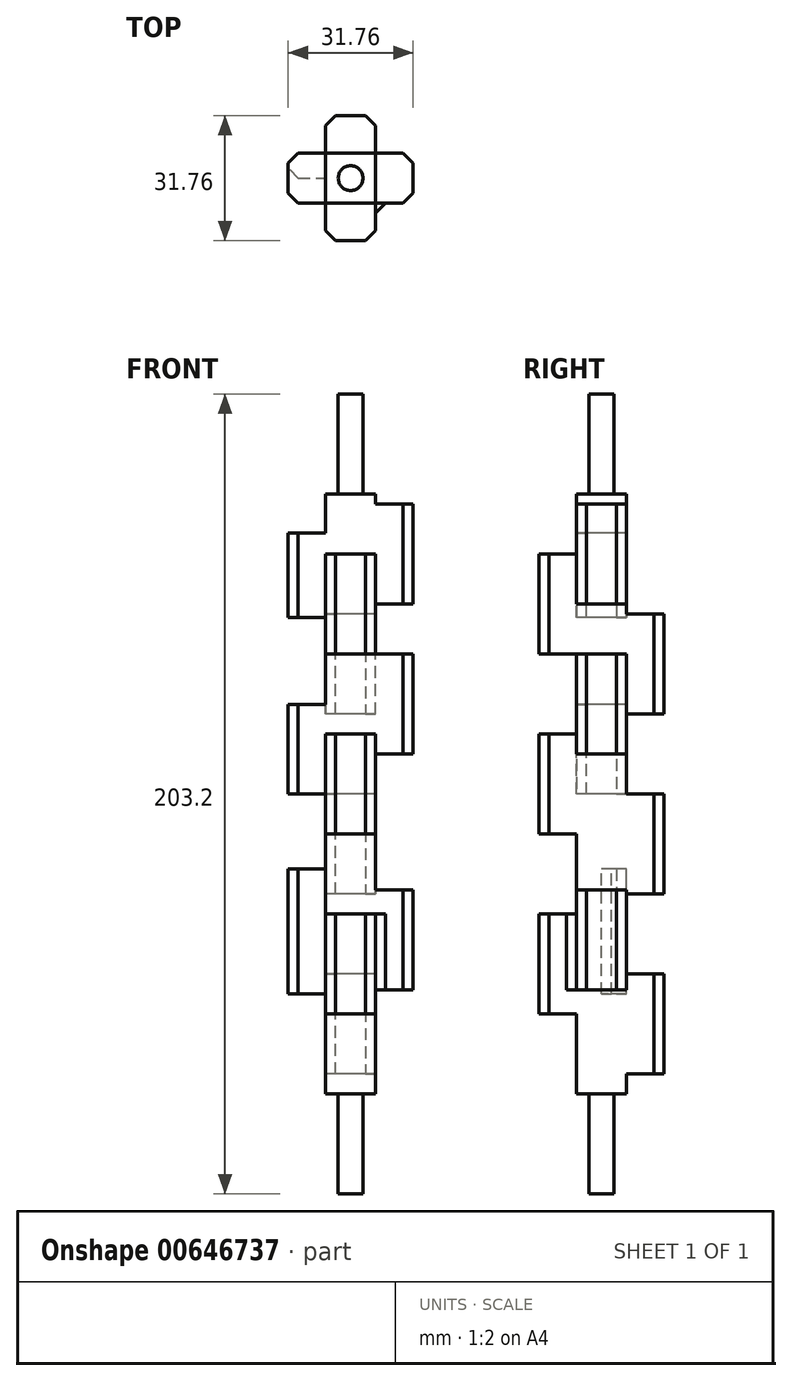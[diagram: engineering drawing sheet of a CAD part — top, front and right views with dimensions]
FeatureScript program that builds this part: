
annotation { "Feature Type Name" : "Feature", "Feature Type Description" : "" }
export const myFeature = defineFeature(function(context is Context, id is Id, definition is map)
    precondition{}
    {
        {
            var Q0;
            Q0=qCreatedBy(makeId("Top.planeOp"),FACE);
            var sketch = newSketch(context, id + "F0", { "sketchPlane" : qUnion([Q0])});
            skLineSegment(sketch, "E0.bottom", {"start": v(6.35, -6.35) * mm, "end": v(-6.35, -6.35) * mm});
            skLineSegment(sketch, "E0.top", {"start": v(6.35, 6.35) * mm, "end": v(-6.35, 6.35) * mm});
            skLineSegment(sketch, "E0.left", {"start": v(6.35, -6.35) * mm, "end": v(6.35, 6.35) * mm});
            skLineSegment(sketch, "E0.right", {"start": v(-6.35, -6.35) * mm, "end": v(-6.35, 6.35) * mm});
            skPoint(sketch, "E0.middle", {"position": v(0, 0) * mm});
            skSolve(sketch);
        }
        {
            var Q0;
            Q0=makeQuery(id+"F0.imprint","IMPRINT",FACE,{"disambiguationData":[TD([[makeQuery(id+"F0.imprint","IMPRINT",EDGE,{"derivedFrom":sQuery(id+"F0.wireOp",EDGE,"E0.bottom")}),-1.0]])]});
            extrude(context, id + "F1", {"entities" : qUnion([Q0]), "endBound" : BoundingType.SYMMETRIC, "depth" : 152.4 * mm, "offsetDistance" : 25.4 * mm});
        }
        {
            var Q0;
            Q0=makeQuery(id+"F1.opExtrude","SWEPT_FACE",FACE,{"disambiguationData":[OSD([sQuery(id+"F0.wireOp",EDGE,"E0.top")])]});
            var sketch = newSketch(context, id + "F2", { "sketchPlane" : qUnion([Q0])});
            skLineSegment(sketch, "E1.bottom", {"start": v(-6.35, 45.72) * mm, "end": v(6.35, 45.72) * mm});
            skLineSegment(sketch, "E1.top", {"start": v(-6.35, 20.32) * mm, "end": v(6.35, 20.32) * mm});
            skLineSegment(sketch, "E1.left", {"start": v(-6.35, 45.72) * mm, "end": v(-6.35, 20.32) * mm});
            skLineSegment(sketch, "E1.right", {"start": v(6.35, 45.72) * mm, "end": v(6.35, 20.32) * mm});
            skLineSegment(sketch, "E2.bottom", {"start": v(-6.35, 0) * mm, "end": v(6.35, 0) * mm});
            skLineSegment(sketch, "E2.top", {"start": v(-6.35, -25.4) * mm, "end": v(6.35, -25.4) * mm});
            skLineSegment(sketch, "E2.left", {"start": v(-6.35, 0) * mm, "end": v(-6.35, -25.4) * mm});
            skLineSegment(sketch, "E2.right", {"start": v(6.35, 0) * mm, "end": v(6.35, -25.4) * mm});
            skLineSegment(sketch, "E3.bottom", {"start": v(-6.35, -45.72) * mm, "end": v(6.35, -45.72) * mm});
            skLineSegment(sketch, "E3.top", {"start": v(-6.35, -71.12) * mm, "end": v(6.35, -71.12) * mm});
            skLineSegment(sketch, "E3.left", {"start": v(-6.35, -45.72) * mm, "end": v(-6.35, -71.12) * mm});
            skLineSegment(sketch, "E3.right", {"start": v(6.35, -45.72) * mm, "end": v(6.35, -71.12) * mm});
            skSolve(sketch);
        }
        {
            var Q0;
            Q0=makeQuery(id+"F2.imprint","IMPRINT",FACE,{"disambiguationData":[TD([[makeQuery(id+"F2.imprint","IMPRINT",EDGE,{"derivedFrom":sQuery(id+"F2.wireOp",EDGE,"E3.bottom")}),-1.0]])]});
            var Q1;
            Q1=makeQuery(id+"F2.imprint","IMPRINT",FACE,{"disambiguationData":[TD([[makeQuery(id+"F2.imprint","IMPRINT",EDGE,{"derivedFrom":sQuery(id+"F2.wireOp",EDGE,"E2.bottom")}),-1.0]])]});
            var Q2;
            Q2=makeQuery(id+"F2.imprint","IMPRINT",FACE,{"disambiguationData":[TD([[makeQuery(id+"F2.imprint","IMPRINT",EDGE,{"derivedFrom":sQuery(id+"F2.wireOp",EDGE,"E1.bottom")}),-1.0]])]});
            extrude(context, id + "F3", {"entities" : qUnion([Q0, Q1, Q2]), "operationType" : NewBodyOperationType.ADD, "depth" : 9.52 * mm, "offsetDistance" : 25.4 * mm});
        }
        {
            var Q0;
            Q0=makeQuery(id+"F1.opExtrude","SWEPT_FACE",FACE,{"disambiguationData":[OSD([sQuery(id+"F0.wireOp",EDGE,"E0.bottom")])]});
            var sketch = newSketch(context, id + "F4", { "sketchPlane" : qUnion([Q0])});
            skLineSegment(sketch, "E4.bottom", {"start": v(-6.35, 60.96) * mm, "end": v(6.35, 60.96) * mm});
            skLineSegment(sketch, "E4.top", {"start": v(-6.35, 35.56) * mm, "end": v(6.35, 35.56) * mm});
            skLineSegment(sketch, "E4.left", {"start": v(-6.35, 60.96) * mm, "end": v(-6.35, 35.56) * mm});
            skLineSegment(sketch, "E4.right", {"start": v(6.35, 60.96) * mm, "end": v(6.35, 35.56) * mm});
            skLineSegment(sketch, "E5.bottom", {"start": v(-6.35, 15.24) * mm, "end": v(6.35, 15.24) * mm});
            skLineSegment(sketch, "E5.top", {"start": v(-6.35, -10.16) * mm, "end": v(6.35, -10.16) * mm});
            skLineSegment(sketch, "E5.left", {"start": v(-6.35, 15.24) * mm, "end": v(-6.35, -10.16) * mm});
            skLineSegment(sketch, "E5.right", {"start": v(6.35, 15.24) * mm, "end": v(6.35, -10.16) * mm});
            skLineSegment(sketch, "E6.bottom", {"start": v(-6.35, -30.48) * mm, "end": v(6.35, -30.48) * mm});
            skLineSegment(sketch, "E6.top", {"start": v(-6.35, -55.88) * mm, "end": v(6.35, -55.88) * mm});
            skLineSegment(sketch, "E6.left", {"start": v(-6.35, -30.48) * mm, "end": v(-6.35, -55.88) * mm});
            skLineSegment(sketch, "E6.right", {"start": v(6.35, -30.48) * mm, "end": v(6.35, -55.88) * mm});
            skSolve(sketch);
        }
        {
            var Q0;
            Q0=makeQuery(id+"F4.imprint","IMPRINT",FACE,{"disambiguationData":[TD([[makeQuery(id+"F4.imprint","IMPRINT",EDGE,{"derivedFrom":sQuery(id+"F4.wireOp",EDGE,"E4.bottom")}),-1.0]])]});
            var Q1;
            Q1=makeQuery(id+"F4.imprint","IMPRINT",FACE,{"disambiguationData":[TD([[makeQuery(id+"F4.imprint","IMPRINT",EDGE,{"derivedFrom":sQuery(id+"F4.wireOp",EDGE,"E5.bottom")}),-1.0]])]});
            var Q2;
            Q2=makeQuery(id+"F4.imprint","IMPRINT",FACE,{"disambiguationData":[TD([[makeQuery(id+"F4.imprint","IMPRINT",EDGE,{"derivedFrom":sQuery(id+"F4.wireOp",EDGE,"E6.bottom")}),-1.0]])]});
            extrude(context, id + "F5", {"entities" : qUnion([Q0, Q1, Q2]), "operationType" : NewBodyOperationType.ADD, "depth" : 9.52 * mm, "offsetDistance" : 25.4 * mm});
        }
        {
            var Q0;
            Q0=makeQuery(id+"F5.boolean.opBoolean","MERGE",FACE,{"derivedFrom":[makeQuery(id+"F3.boolean.opBoolean","MERGE",FACE,{"derivedFrom":[makeQuery(id+"F1.opExtrude","SWEPT_FACE",FACE,{"disambiguationData":[OSD([sQuery(id+"F0.wireOp",EDGE,"E0.right")])]}),makeQuery(id+"F3.opExtrude","SWEPT_FACE",FACE,{"disambiguationData":[OSD([sQuery(id+"F2.wireOp",EDGE,"E1.right")])]}),makeQuery(id+"F3.opExtrude","SWEPT_FACE",FACE,{"disambiguationData":[OSD([sQuery(id+"F2.wireOp",EDGE,"E2.right")])]}),makeQuery(id+"F3.opExtrude","SWEPT_FACE",FACE,{"disambiguationData":[OSD([sQuery(id+"F2.wireOp",EDGE,"E3.right")])]})]}),makeQuery(id+"F5.opExtrude","SWEPT_FACE",FACE,{"disambiguationData":[OSD([sQuery(id+"F4.wireOp",EDGE,"E4.left")])]}),makeQuery(id+"F5.opExtrude","SWEPT_FACE",FACE,{"disambiguationData":[OSD([sQuery(id+"F4.wireOp",EDGE,"E5.left")])]}),makeQuery(id+"F5.opExtrude","SWEPT_FACE",FACE,{"disambiguationData":[OSD([sQuery(id+"F4.wireOp",EDGE,"E6.left")])]})]});
            var sketch = newSketch(context, id + "F6", { "sketchPlane" : qUnion([Q0])});
            skLineSegment(sketch, "E7.bottom", {"start": v(-6.35, -50.8) * mm, "end": v(0, -50.8) * mm});
            skLineSegment(sketch, "E7.top", {"start": v(-6.35, -19.05) * mm, "end": v(0, -19.05) * mm});
            skLineSegment(sketch, "E7.left", {"start": v(-6.35, -50.8) * mm, "end": v(-6.35, -19.05) * mm});
            skLineSegment(sketch, "E7.right", {"start": v(0, -50.8) * mm, "end": v(0, -19.05) * mm});
            skLineSegment(sketch, "E8.bottom", {"start": v(-6.35, 0) * mm, "end": v(6.35, 0) * mm});
            skLineSegment(sketch, "E8.top", {"start": v(-6.35, 22.71) * mm, "end": v(6.35, 22.71) * mm});
            skLineSegment(sketch, "E8.left", {"start": v(-6.35, 0) * mm, "end": v(-6.35, 22.71) * mm});
            skLineSegment(sketch, "E8.right", {"start": v(6.35, 0) * mm, "end": v(6.35, 22.71) * mm});
            skLineSegment(sketch, "E9.bottom", {"start": v(-6.35, 44.79) * mm, "end": v(6.35, 44.79) * mm});
            skLineSegment(sketch, "E9.top", {"start": v(-6.35, 66.26) * mm, "end": v(6.35, 66.26) * mm});
            skLineSegment(sketch, "E9.left", {"start": v(-6.35, 44.79) * mm, "end": v(-6.35, 66.26) * mm});
            skLineSegment(sketch, "E9.right", {"start": v(6.35, 44.79) * mm, "end": v(6.35, 66.26) * mm});
            skSolve(sketch);
        }
        {
            var Q0;
            {var subQ13=sQuery(id+"F6.wireOp",EDGE,"E9.bottom");Q0=makeQuery(id+"F6.imprint","IMPRINT",FACE,{"disambiguationData":[TD([[makeQuery(id+"F6.imprint","IMPRINT",EDGE,{"derivedFrom":subQ13}),1.0]])]});}
            var Q1;
            {var subQ5=sQuery(id+"F6.wireOp",EDGE,"E8.bottom");Q1=makeQuery(id+"F6.imprint","IMPRINT",FACE,{"disambiguationData":[TD([[makeQuery(id+"F6.imprint","IMPRINT",EDGE,{"derivedFrom":subQ5}),1.0]])]});}
            var Q2;
            {var subQ6=sQuery(id+"F6.wireOp",EDGE,"E7.bottom");Q2=makeQuery(id+"F6.imprint","IMPRINT",FACE,{"disambiguationData":[TD([[makeQuery(id+"F6.imprint","IMPRINT",EDGE,{"derivedFrom":subQ6}),1.0]])]});}
            extrude(context, id + "F7", {"entities" : qUnion([Q0, Q1, Q2]), "operationType" : NewBodyOperationType.ADD, "depth" : 9.52 * mm, "offsetDistance" : 25.4 * mm});
        }
        {
            var Q0;
            Q0=makeQuery(id+"F5.boolean.opBoolean","MERGE",FACE,{"derivedFrom":[makeQuery(id+"F3.boolean.opBoolean","MERGE",FACE,{"derivedFrom":[makeQuery(id+"F1.opExtrude","SWEPT_FACE",FACE,{"disambiguationData":[OSD([sQuery(id+"F0.wireOp",EDGE,"E0.left")])]}),makeQuery(id+"F3.opExtrude","SWEPT_FACE",FACE,{"disambiguationData":[OSD([sQuery(id+"F2.wireOp",EDGE,"E1.left")])]}),makeQuery(id+"F3.opExtrude","SWEPT_FACE",FACE,{"disambiguationData":[OSD([sQuery(id+"F2.wireOp",EDGE,"E2.left")])]}),makeQuery(id+"F3.opExtrude","SWEPT_FACE",FACE,{"disambiguationData":[OSD([sQuery(id+"F2.wireOp",EDGE,"E3.left")])]})]}),makeQuery(id+"F5.opExtrude","SWEPT_FACE",FACE,{"disambiguationData":[OSD([sQuery(id+"F4.wireOp",EDGE,"E4.right")])]}),makeQuery(id+"F5.opExtrude","SWEPT_FACE",FACE,{"disambiguationData":[OSD([sQuery(id+"F4.wireOp",EDGE,"E5.right")])]}),makeQuery(id+"F5.opExtrude","SWEPT_FACE",FACE,{"disambiguationData":[OSD([sQuery(id+"F4.wireOp",EDGE,"E6.right")])]})]});
            var sketch = newSketch(context, id + "F8", { "sketchPlane" : qUnion([Q0])});
            skPoint(sketch, "E10.oppositeSnap0", {"position": v(6.35, 60.96) * mm});
            skLineSegment(sketch, "E10.bottom", {"start": v(-6.35, 73.66) * mm, "end": v(6.35, 73.66) * mm});
            skLineSegment(sketch, "E10.top", {"start": v(-6.35, 48.26) * mm, "end": v(6.35, 48.26) * mm});
            skLineSegment(sketch, "E10.left", {"start": v(-6.35, 73.66) * mm, "end": v(-6.35, 48.26) * mm});
            skLineSegment(sketch, "E10.right", {"start": v(6.35, 73.66) * mm, "end": v(6.35, 48.26) * mm});
            skLineSegment(sketch, "E11.bottom", {"start": v(6.35, 10.16) * mm, "end": v(-6.35, 10.16) * mm});
            skLineSegment(sketch, "E11.top", {"start": v(6.35, 35.56) * mm, "end": v(-6.35, 35.56) * mm});
            skLineSegment(sketch, "E11.left", {"start": v(6.35, 10.16) * mm, "end": v(6.35, 35.56) * mm});
            skLineSegment(sketch, "E11.right", {"start": v(-6.35, 10.16) * mm, "end": v(-6.35, 35.56) * mm});
            skLineSegment(sketch, "E12.bottom", {"start": v(-6.35, -24.37) * mm, "end": v(6.35, -24.37) * mm});
            skLineSegment(sketch, "E12.top", {"start": v(-6.35, -49.77) * mm, "end": v(6.35, -49.77) * mm});
            skLineSegment(sketch, "E12.left", {"start": v(-6.35, -24.37) * mm, "end": v(-6.35, -49.77) * mm});
            skLineSegment(sketch, "E12.right", {"start": v(6.35, -24.37) * mm, "end": v(6.35, -49.77) * mm});
            skSolve(sketch);
        }
        {
            var Q0;
            {var subQ6=sQuery(id+"F8.wireOp",EDGE,"E12.bottom");Q0=makeQuery(id+"F8.imprint","IMPRINT",FACE,{"disambiguationData":[TD([[makeQuery(id+"F8.imprint","IMPRINT",EDGE,{"derivedFrom":subQ6}),-1.0]])]});}
            var Q1;
            {var subQ6=sQuery(id+"F8.wireOp",EDGE,"E11.bottom");Q1=makeQuery(id+"F8.imprint","IMPRINT",FACE,{"disambiguationData":[TD([[makeQuery(id+"F8.imprint","IMPRINT",EDGE,{"derivedFrom":subQ6}),-1.0]])]});}
            var Q2;
            {var subQ6=sQuery(id+"F8.wireOp",EDGE,"E10.bottom");Q2=makeQuery(id+"F8.imprint","IMPRINT",FACE,{"disambiguationData":[TD([[makeQuery(id+"F8.imprint","IMPRINT",EDGE,{"derivedFrom":subQ6}),-1.0]])]});}
            extrude(context, id + "F9", {"entities" : qUnion([Q0, Q1, Q2]), "operationType" : NewBodyOperationType.ADD, "depth" : 9.52 * mm, "offsetDistance" : 25.4 * mm});
        }
        {
            var Q0;
            Q0=makeQuery(id+"F1.opExtrude","CAP_FACE",FACE,{"disambiguationData":[OSD([sQuery(id+"F0.wireOp",EDGE,"E0.bottom"),sQuery(id+"F0.wireOp",EDGE,"E0.top"),sQuery(id+"F0.wireOp",EDGE,"E0.left"),sQuery(id+"F0.wireOp",EDGE,"E0.right")])],"isStart":true});
            var sketch = newSketch(context, id + "F10", { "sketchPlane" : qUnion([Q0])});
            skCircle(sketch, "E13", {"center": v(0, 0) * mm, "radius": 3.15 * mm});
            skSolve(sketch);
        }
        {
            var Q0;
            Q0=makeQuery(id+"F10.imprint","IMPRINT",FACE,{"disambiguationData":[TD([[makeQuery(id+"F10.imprint","IMPRINT",EDGE,{"derivedFrom":sQuery(id+"F10.wireOp",EDGE,"E13")}),1.0]])]});
            extrude(context, id + "F11", {"entities" : qUnion([Q0]), "operationType" : NewBodyOperationType.ADD, "depth" : 25.4 * mm, "offsetDistance" : 25.4 * mm});
        }
        {
            var Q0;
            Q0=makeQuery(id+"F1.opExtrude","CAP_FACE",FACE,{"disambiguationData":[OSD([sQuery(id+"F0.wireOp",EDGE,"E0.bottom"),sQuery(id+"F0.wireOp",EDGE,"E0.top"),sQuery(id+"F0.wireOp",EDGE,"E0.left"),sQuery(id+"F0.wireOp",EDGE,"E0.right")])],"isStart":false});
            var sketch = newSketch(context, id + "F12", { "sketchPlane" : qUnion([Q0])});
            skCircle(sketch, "E14", {"center": v(0, 0) * mm, "radius": 3.15 * mm});
            skSolve(sketch);
        }
        {
            var Q0;
            Q0=makeQuery(id+"F12.imprint","IMPRINT",FACE,{"disambiguationData":[TD([[makeQuery(id+"F12.imprint","IMPRINT",EDGE,{"derivedFrom":sQuery(id+"F12.wireOp",EDGE,"E14")}),1.0]])]});
            extrude(context, id + "F13", {"entities" : qUnion([Q0]), "operationType" : NewBodyOperationType.ADD, "depth" : 25.4 * mm, "offsetDistance" : 25.4 * mm});
        }
        {
            var Q0;
            Q0=makeQuery(id+"F9.opExtrude","CAP_EDGE",EDGE,{"disambiguationData":[OSD([sQuery(id+"F8.wireOp",EDGE,"E10.left")])],"isStart":false});
            var Q1;
            Q1=makeQuery(id+"F9.opExtrude","CAP_EDGE",EDGE,{"disambiguationData":[OSD([sQuery(id+"F8.wireOp",EDGE,"E10.right")])],"isStart":false});
            var Q2;
            Q2=makeQuery(id+"F5.opExtrude","CAP_EDGE",EDGE,{"disambiguationData":[OSD([sQuery(id+"F4.wireOp",EDGE,"E4.right")])],"isStart":false});
            var Q3;
            Q3=makeQuery(id+"F5.opExtrude","CAP_EDGE",EDGE,{"disambiguationData":[OSD([sQuery(id+"F4.wireOp",EDGE,"E4.left")])],"isStart":false});
            var Q4;
            Q4=makeQuery(id+"F7.opExtrude","CAP_EDGE",EDGE,{"disambiguationData":[OSD([sQuery(id+"F6.wireOp",EDGE,"E9.right")])],"isStart":false});
            var Q5;
            Q5=makeQuery(id+"F7.opExtrude","CAP_EDGE",EDGE,{"disambiguationData":[OSD([sQuery(id+"F6.wireOp",EDGE,"E9.left")])],"isStart":false});
            var Q6;
            Q6=makeQuery(id+"F3.opExtrude","CAP_EDGE",EDGE,{"disambiguationData":[OSD([sQuery(id+"F2.wireOp",EDGE,"E1.right")])],"isStart":false});
            var Q7;
            Q7=makeQuery(id+"F3.opExtrude","CAP_EDGE",EDGE,{"disambiguationData":[OSD([sQuery(id+"F2.wireOp",EDGE,"E1.left")])],"isStart":false});
            var Q8;
            Q8=makeQuery(id+"F9.opExtrude","CAP_EDGE",EDGE,{"disambiguationData":[OSD([sQuery(id+"F8.wireOp",EDGE,"E11.left")])],"isStart":false});
            var Q9;
            Q9=makeQuery(id+"F9.opExtrude","CAP_EDGE",EDGE,{"disambiguationData":[OSD([sQuery(id+"F8.wireOp",EDGE,"E11.right")])],"isStart":false});
            var Q10;
            Q10=makeQuery(id+"F5.opExtrude","CAP_EDGE",EDGE,{"disambiguationData":[OSD([sQuery(id+"F4.wireOp",EDGE,"E5.right")])],"isStart":false});
            var Q11;
            Q11=makeQuery(id+"F5.opExtrude","CAP_EDGE",EDGE,{"disambiguationData":[OSD([sQuery(id+"F4.wireOp",EDGE,"E5.left")])],"isStart":false});
            var Q12;
            Q12=makeQuery(id+"F7.opExtrude","CAP_EDGE",EDGE,{"disambiguationData":[OSD([sQuery(id+"F6.wireOp",EDGE,"E8.right")])],"isStart":false});
            var Q13;
            Q13=makeQuery(id+"F7.opExtrude","CAP_EDGE",EDGE,{"disambiguationData":[OSD([sQuery(id+"F6.wireOp",EDGE,"E8.left")])],"isStart":false});
            var Q14;
            Q14=makeQuery(id+"F3.opExtrude","CAP_EDGE",EDGE,{"disambiguationData":[OSD([sQuery(id+"F2.wireOp",EDGE,"E2.right")])],"isStart":false});
            var Q15;
            Q15=makeQuery(id+"F3.opExtrude","CAP_EDGE",EDGE,{"disambiguationData":[OSD([sQuery(id+"F2.wireOp",EDGE,"E2.left")])],"isStart":false});
            var Q16;
            Q16=makeQuery(id+"F7.opExtrude","CAP_EDGE",EDGE,{"disambiguationData":[OSD([sQuery(id+"F6.wireOp",EDGE,"E7.left")])],"isStart":false});
            var Q17;
            Q17=makeQuery(id+"F7.opExtrude","CAP_EDGE",EDGE,{"disambiguationData":[OSD([sQuery(id+"F6.wireOp",EDGE,"E7.right")])],"isStart":false});
            var Q18;
            Q18=makeQuery(id+"F5.opExtrude","CAP_EDGE",EDGE,{"disambiguationData":[OSD([sQuery(id+"F4.wireOp",EDGE,"E6.left")])],"isStart":false});
            var Q19;
            Q19=makeQuery(id+"F5.opExtrude","CAP_EDGE",EDGE,{"disambiguationData":[OSD([sQuery(id+"F4.wireOp",EDGE,"E6.right")])],"isStart":false});
            var Q20;
            Q20=makeQuery(id+"F9.opExtrude","CAP_EDGE",EDGE,{"disambiguationData":[OSD([sQuery(id+"F8.wireOp",EDGE,"E12.left")])],"isStart":true});
            var Q21;
            Q21=makeQuery(id+"F9.opExtrude","CAP_EDGE",EDGE,{"disambiguationData":[OSD([sQuery(id+"F8.wireOp",EDGE,"E12.right")])],"isStart":false});
            var Q22;
            Q22=makeQuery(id+"F9.opExtrude","CAP_EDGE",EDGE,{"disambiguationData":[OSD([sQuery(id+"F8.wireOp",EDGE,"E12.left")])],"isStart":false});
            var Q23;
            Q23=makeQuery(id+"F3.opExtrude","CAP_EDGE",EDGE,{"disambiguationData":[OSD([sQuery(id+"F2.wireOp",EDGE,"E3.left")])],"isStart":false});
            var Q24;
            Q24=makeQuery(id+"F3.opExtrude","CAP_EDGE",EDGE,{"disambiguationData":[OSD([sQuery(id+"F2.wireOp",EDGE,"E3.right")])],"isStart":false});
            chamfer(context, id + "F14", {"entities" : qUnion([Q0, Q1, Q2, Q3, Q4, Q5, Q6, Q7, Q8, Q9, Q10, Q11, Q12, Q13, Q14, Q15, Q16, Q17, Q18, Q19, Q20, Q21, Q22, Q23, Q24]), "width" : 2.54 * mm, "tangentPropagation" : true});
        }
    });
